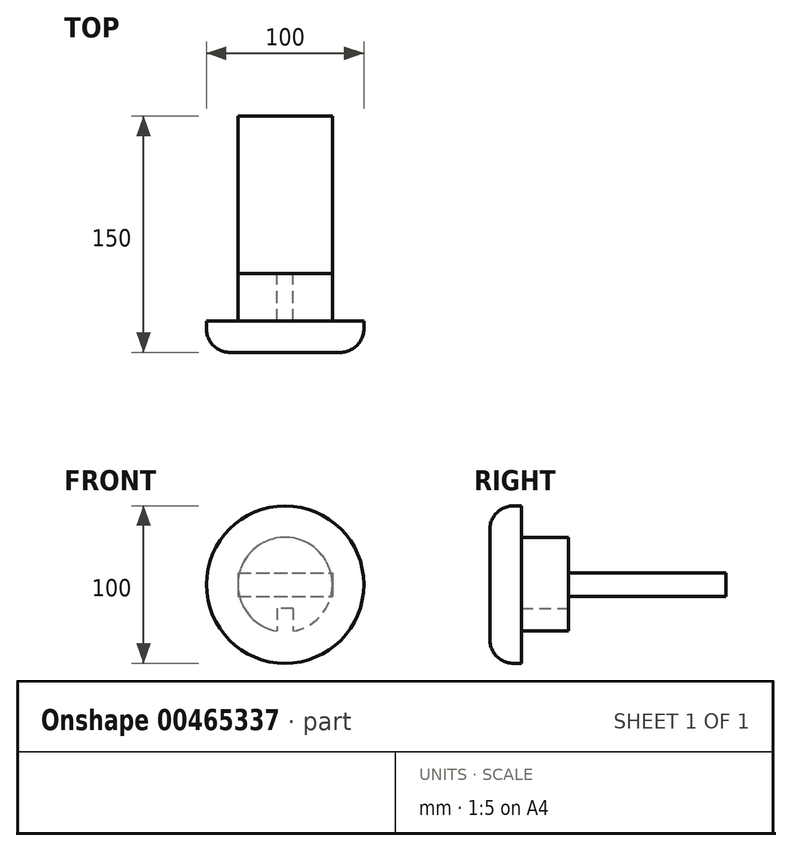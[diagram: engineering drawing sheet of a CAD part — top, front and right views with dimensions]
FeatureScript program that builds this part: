
annotation { "Feature Type Name" : "Feature", "Feature Type Description" : "" }
export const myFeature = defineFeature(function(context is Context, id is Id, definition is map)
    precondition{}
    {
        {
            var Q0;
            Q0=qCreatedBy(makeId("Front.planeOp"),FACE);
            var sketch = newSketch(context, id + "F0", { "sketchPlane" : qUnion([Q0])});
            skLineSegment(sketch, "E0.bottom", {"start": v(-30, 7.5) * mm, "end": v(30, 7.5) * mm});
            skLineSegment(sketch, "E0.top", {"start": v(-30, -7.5) * mm, "end": v(30, -7.5) * mm});
            skLineSegment(sketch, "E0.left", {"start": v(-30, 7.5) * mm, "end": v(-30, -7.5) * mm});
            skLineSegment(sketch, "E0.right", {"start": v(30, 7.5) * mm, "end": v(30, -7.5) * mm});
            skSolve(sketch);
        }
        {
            var Q0;
            Q0=makeQuery(id+"F0.imprint","IMPRINT",FACE,{"disambiguationData":[TD([[makeQuery(id+"F0.imprint","IMPRINT",EDGE,{"derivedFrom":sQuery(id+"F0.wireOp",EDGE,"E0.bottom")}),-1.0]])]});
            extrude(context, id + "F1", {"entities" : qUnion([Q0]), "oppositeDirection" : true, "depth" : 100 * mm});
        }
        {
            var Q0;
            Q0=makeQuery(id+"F1.opExtrude","CAP_FACE",FACE,{"disambiguationData":[OSD([sQuery(id+"F0.wireOp",EDGE,"E0.bottom"),sQuery(id+"F0.wireOp",EDGE,"E0.top"),sQuery(id+"F0.wireOp",EDGE,"E0.left"),sQuery(id+"F0.wireOp",EDGE,"E0.right")])],"isStart":true});
            var sketch = newSketch(context, id + "F2", { "sketchPlane" : qUnion([Q0])});
            skCircle(sketch, "E1", {"center": v(0, 0) * mm, "radius": 30 * mm});
            skSolve(sketch);
        }
        {
            var Q0;
            {var subQ0=sQuery(id+"F2.wireOp",EDGE,"E1");var subQ1=makeQuery(id+"F1.opExtrude","CAP_EDGE",EDGE,{"disambiguationData":[OSD([sQuery(id+"F0.wireOp",EDGE,"E0.bottom")])],"isStart":true});var subQ2=makeQuery(id+"F2.imprint","INTERSECT",VERTEX,{"disambiguationData":[OD(0.0)],"derivedFrom":[subQ1,subQ0]});Q0=makeQuery(id+"F2.imprint","IMPRINT",FACE,{"disambiguationData":[TD([[makeQuery(id+"F2.imprint","IMPRINT",EDGE,{"disambiguationData":[TD([[subQ2,-1.0]])],"derivedFrom":subQ0}),1.0]])]});}
            var Q1;
            {var subQ0=sQuery(id+"F2.wireOp",EDGE,"E1");var subQ4=makeQuery(id+"F1.opExtrude","CAP_EDGE",EDGE,{"disambiguationData":[OSD([sQuery(id+"F0.wireOp",EDGE,"E0.bottom")])],"isStart":true});var subQ8=makeQuery(id+"F2.imprint","INTERSECT",VERTEX,{"disambiguationData":[OD(0.0)],"derivedFrom":[subQ4,subQ0]});Q1=makeQuery(id+"F2.imprint","IMPRINT",FACE,{"disambiguationData":[TD([[makeQuery(id+"F2.imprint","IMPRINT",EDGE,{"disambiguationData":[TD([[subQ8,1.0]])],"derivedFrom":subQ0}),1.0]])]});}
            var Q2;
            {var subQ0=sQuery(id+"F2.wireOp",EDGE,"E1");var subQ1=makeQuery(id+"F1.opExtrude","CAP_EDGE",EDGE,{"disambiguationData":[OSD([sQuery(id+"F0.wireOp",EDGE,"E0.top")])],"isStart":true});var subQ2=makeQuery(id+"F2.imprint","INTERSECT",VERTEX,{"disambiguationData":[OD(0.0)],"derivedFrom":[subQ1,subQ0]});Q2=makeQuery(id+"F2.imprint","IMPRINT",FACE,{"disambiguationData":[TD([[makeQuery(id+"F2.imprint","IMPRINT",EDGE,{"disambiguationData":[TD([[subQ2,-1.0]])],"derivedFrom":subQ0}),1.0]])]});}
            extrude(context, id + "F3", {"entities" : qUnion([Q0, Q1, Q2]), "operationType" : NewBodyOperationType.ADD, "depth" : 30 * mm});
        }
        {
            var Q0;
            Q0=makeQuery(id+"F3.opExtrude","CAP_FACE",FACE,{"disambiguationData":[OSD([sQuery(id+"F2.wireOp",EDGE,"E1")])],"isStart":false});
            var sketch = newSketch(context, id + "F4", { "sketchPlane" : qUnion([Q0])});
            skCircle(sketch, "E2.0", {"center": v(0, 0) * mm, "radius": 50 * mm});
            skSolve(sketch);
        }
        {
            var Q0;
            Q0=makeQuery(id+"F4.imprint","IMPRINT",FACE,{"disambiguationData":[TD([[makeQuery(id+"F4.imprint","IMPRINT",EDGE,{"derivedFrom":makeQuery(id+"F3.opExtrude","CAP_EDGE",EDGE,{"disambiguationData":[OSD([sQuery(id+"F2.wireOp",EDGE,"E1")])],"isStart":false})}),1.0]])]});
            var Q1;
            Q1=makeQuery(id+"F4.imprint","IMPRINT",FACE,{"disambiguationData":[TD([[makeQuery(id+"F4.imprint","IMPRINT",EDGE,{"derivedFrom":sQuery(id+"F4.wireOp",EDGE,"E2.0")}),1.0]])]});
            extrude(context, id + "F5", {"entities" : qUnion([Q0, Q1]), "operationType" : NewBodyOperationType.ADD, "depth" : 20 * mm});
        }
        {
            var Q0;
            Q0=makeQuery(id+"F5.opExtrude","CAP_EDGE",EDGE,{"disambiguationData":[OSD([sQuery(id+"F4.wireOp",EDGE,"E2.0")])],"isStart":false});
            fillet(context, id + "F6", {"entities" : qUnion([Q0]), "radius" : 15 * mm, "tangentPropagation" : true, "allowEdgeOverflow" : false});
        }
        {
            var Q0;
            {var subQ0=sQuery(id+"F0.wireOp",EDGE,"E0.top");var subQ1=sQuery(id+"F2.wireOp",EDGE,"E1");Q0=makeQuery(id+"F3.boolean.opBoolean","SPLIT",FACE,{"disambiguationData":[TD([makeQuery(id+"F1.opExtrude","SWEPT_FACE",FACE,{"disambiguationData":[OSD([subQ0])]})])],"derivedFrom":makeQuery(id+"F3.opExtrude","CAP_FACE",FACE,{"disambiguationData":[OSD([subQ1])],"isStart":true})});}
            var sketch = newSketch(context, id + "F7", { "sketchPlane" : qUnion([Q0])});
            skLineSegment(sketch, "E3.bottom", {"start": v(-5, -15) * mm, "end": v(5, -15) * mm});
            skLineSegment(sketch, "E3.top", {"start": v(-5, -35) * mm, "end": v(5, -35) * mm});
            skLineSegment(sketch, "E3.left", {"start": v(-5, -15) * mm, "end": v(-5, -35) * mm});
            skLineSegment(sketch, "E3.right", {"start": v(5, -15) * mm, "end": v(5, -35) * mm});
            skSolve(sketch);
        }
        {
            var Q0;
            {var subQ0=sQuery(id+"F7.wireOp",EDGE,"E3.bottom");Q0=makeQuery(id+"F7.imprint","IMPRINT",FACE,{"disambiguationData":[TD([[makeQuery(id+"F7.imprint","IMPRINT",EDGE,{"derivedFrom":subQ0}),-1.0]])]});}
            var Q1;
            {var subQ0=sQuery(id+"F7.wireOp",EDGE,"5PyZKUXV-9kCO-iEmy-CBHk-ocQjQXtH8eNn");Q1=makeQuery(id+"F7.imprint","IMPRINT",FACE,{"disambiguationData":[TD([[makeQuery(id+"F7.imprint","IMPRINT",EDGE,{"derivedFrom":subQ0}),1.0]])]});}
            var Q2;
            {var subQ2=sQuery(id+"F7.wireOp",EDGE,"GAfvIhGV-mibL-YIyv-Vovn-iUNGzplh9J49");Q2=makeQuery(id+"F7.imprint","IMPRINT",FACE,{"disambiguationData":[TD([[makeQuery(id+"F7.imprint","IMPRINT",EDGE,{"derivedFrom":subQ2}),1.0]])]});}
            extrude(context, id + "F8", {"entities" : qUnion([Q0, Q1, Q2]), "operationType" : NewBodyOperationType.REMOVE, "oppositeDirection" : true, "depth" : 30 * mm});
        }
    });
